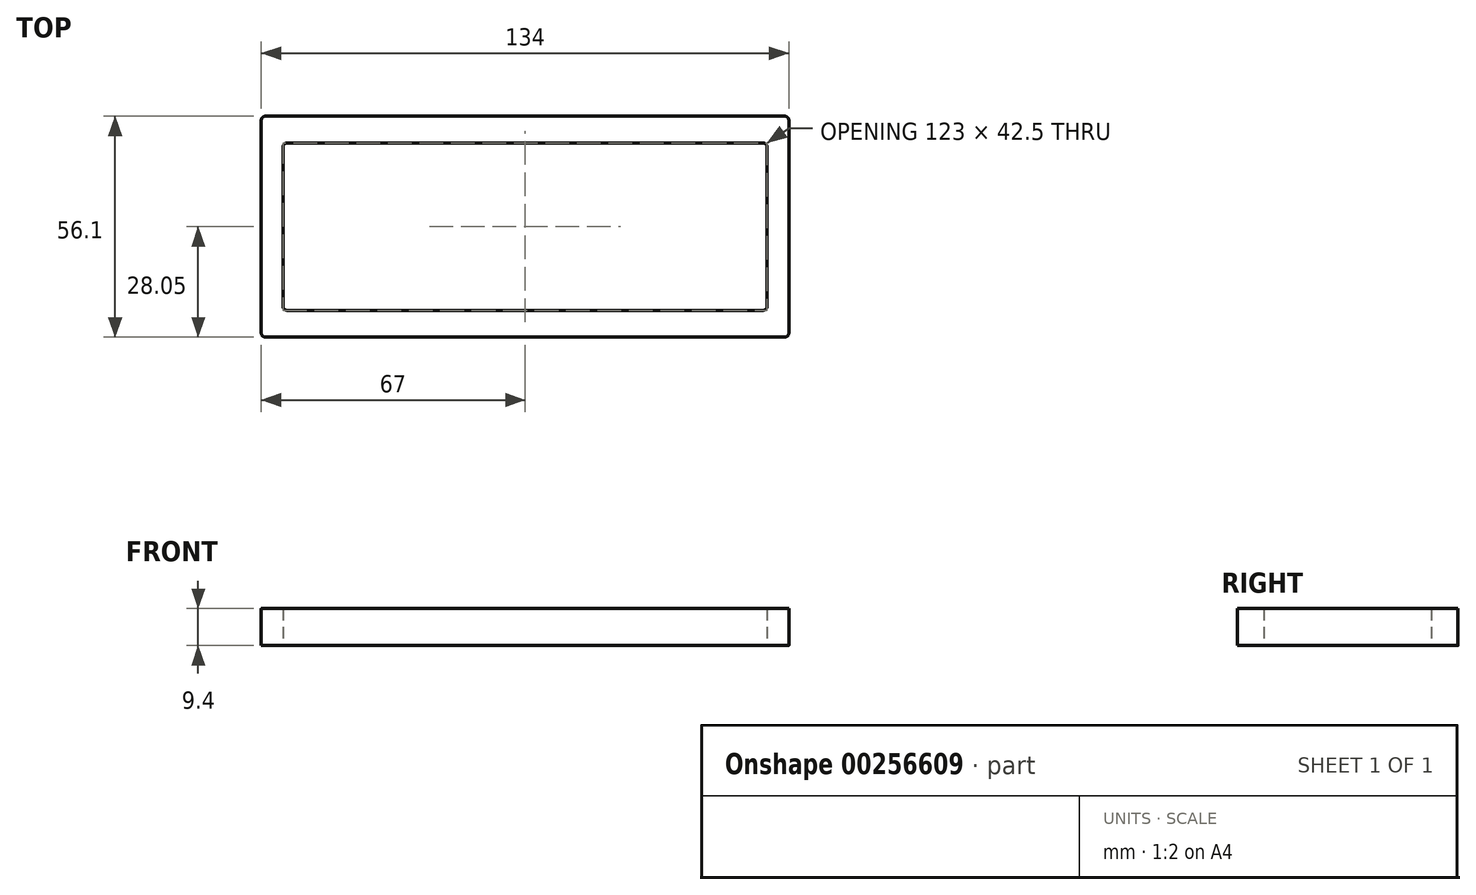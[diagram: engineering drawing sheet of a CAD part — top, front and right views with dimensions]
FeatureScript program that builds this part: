
annotation { "Feature Type Name" : "Feature", "Feature Type Description" : "" }
export const myFeature = defineFeature(function(context is Context, id is Id, definition is map)
    precondition{}
    {
        {
            var Q0;
            Q0=qCreatedBy(makeId("Top.planeOp"),FACE);
            var sketch = newSketch(context, id + "F0", { "sketchPlane" : qUnion([Q0])});
            skLineSegment(sketch, "E0.bottom", {"start": v(66, -28.05) * mm, "end": v(-66, -28.05) * mm});
            skLineSegment(sketch, "E0.top", {"start": v(66, 28.05) * mm, "end": v(-66, 28.05) * mm});
            skLineSegment(sketch, "E0.left", {"start": v(67, -27.05) * mm, "end": v(67, 27.05) * mm});
            skLineSegment(sketch, "E0.right", {"start": v(-67, -27.05) * mm, "end": v(-67, 27.05) * mm});
            skPoint(sketch, "E0.middle", {"position": v(0, 0) * mm});
            skLineSegment(sketch, "E1.bottom", {"start": v(60.5, -21.25) * mm, "end": v(-60.5, -21.25) * mm});
            skLineSegment(sketch, "E1.top", {"start": v(60.5, 21.25) * mm, "end": v(-60.5, 21.25) * mm});
            skLineSegment(sketch, "E1.left", {"start": v(61.5, -20.25) * mm, "end": v(61.5, 20.25) * mm});
            skLineSegment(sketch, "E1.right", {"start": v(-61.5, -20.25) * mm, "end": v(-61.5, 20.25) * mm});
            skPoint(sketch, "E2.visualSharp", {"position": v(-67, -28.05) * mm});
            skArc(sketch, "E2.filletArc", {"start": v(-67, -27.05) * mm, "mid": v(-66.7, -27.76) * mm, "end": v(-66, -28.05) * mm});
            skPoint(sketch, "E3.visualSharp", {"position": v(-67, 28.05) * mm});
            skArc(sketch, "E3.filletArc", {"start": v(-66, 28.05) * mm, "mid": v(-66.7, 27.76) * mm, "end": v(-67, 27.05) * mm});
            skPoint(sketch, "E4.visualSharp", {"position": v(67, 28.05) * mm});
            skArc(sketch, "E4.filletArc", {"start": v(67, 27.05) * mm, "mid": v(66.7, 27.76) * mm, "end": v(66, 28.05) * mm});
            skPoint(sketch, "E5.visualSharp", {"position": v(67, -28.05) * mm});
            skArc(sketch, "E5.filletArc", {"start": v(66, -28.05) * mm, "mid": v(66.7, -27.76) * mm, "end": v(67, -27.05) * mm});
            skPoint(sketch, "E6.visualSharp", {"position": v(-61.5, -21.25) * mm});
            skArc(sketch, "E6.filletArc", {"start": v(-61.5, -20.25) * mm, "mid": v(-61.2, -20.96) * mm, "end": v(-60.5, -21.25) * mm});
            skPoint(sketch, "E7.visualSharp", {"position": v(-61.5, 21.25) * mm});
            skArc(sketch, "E7.filletArc", {"start": v(-60.5, 21.25) * mm, "mid": v(-61.2, 20.96) * mm, "end": v(-61.5, 20.25) * mm});
            skPoint(sketch, "E8.visualSharp", {"position": v(61.5, 21.25) * mm});
            skArc(sketch, "E8.filletArc", {"start": v(61.5, 20.25) * mm, "mid": v(61.2, 20.96) * mm, "end": v(60.5, 21.25) * mm});
            skPoint(sketch, "E9.visualSharp", {"position": v(61.5, -21.25) * mm});
            skArc(sketch, "E9.filletArc", {"start": v(60.5, -21.25) * mm, "mid": v(61.2, -20.96) * mm, "end": v(61.5, -20.25) * mm});
            skSolve(sketch);
        }
        {
            var Q0;
            Q0=makeQuery(id+"F0.imprint","IMPRINT",FACE,{"disambiguationData":[TD([[makeQuery(id+"F0.imprint","IMPRINT",EDGE,{"derivedFrom":sQuery(id+"F0.wireOp",EDGE,"E0.bottom")}),-1.0]])]});
            extrude(context, id + "F1", {"entities" : qUnion([Q0]), "depth" : 9.4 * mm});
        }
    });
